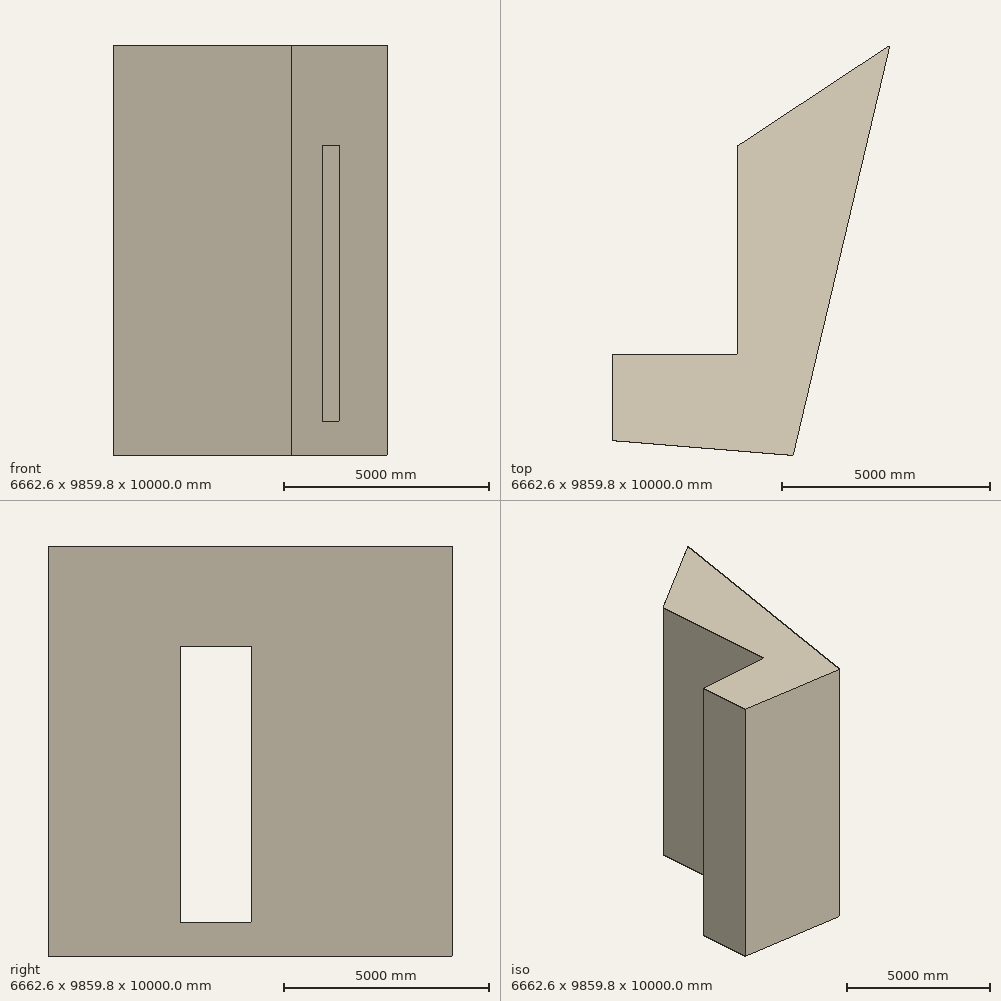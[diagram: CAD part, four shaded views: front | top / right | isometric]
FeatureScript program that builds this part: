
annotation { "Feature Type Name" : "Feature", "Feature Type Description" : "" }
export const myFeature = defineFeature(function(context is Context, id is Id, definition is map)
    precondition{}
    {
        {
            var Q0;
            Q0=qCreatedBy(makeId("Top.planeOp"),FACE);
            var sketch = newSketch(context, id + "F0", { "sketchPlane" : qUnion([Q0])});
            skLineSegment(sketch, "E0.bottom", {"start": v(-10975.18, 7041.84) * mm, "end": v(13954.74, 7041.84) * mm});
            skLineSegment(sketch, "E0.top", {"start": v(-13975.18, -7051.86) * mm, "end": v(13954.74, -7051.86) * mm});
            skLineSegment(sketch, "E0.left", {"start": v(-13975.18, 2041.84) * mm, "end": v(-13975.18, -7051.86) * mm});
            skLineSegment(sketch, "E0.right", {"start": v(13954.74, 7041.84) * mm, "end": v(13954.74, -7051.86) * mm});
            skLineSegment(sketch, "E1", {"start": v(-10975.18, 7041.84) * mm, "end": v(-10975.18, 2041.84) * mm});
            skLineSegment(sketch, "E2", {"start": v(-10975.18, 2041.84) * mm, "end": v(-13975.18, 2041.84) * mm});
            skLineSegment(sketch, "E3.bottom", {"start": v(-12681.6, 1707.23) * mm, "end": v(-3728.69, 1707.23) * mm});
            skLineSegment(sketch, "E3.top", {"start": v(-13445.3, -6384.52) * mm, "end": v(-3728.69, -6384.52) * mm});
            skLineSegment(sketch, "E3.left", {"start": v(-13445.3, 1037.52) * mm, "end": v(-13445.3, -6384.52) * mm});
            skLineSegment(sketch, "E3.right", {"start": v(-3728.69, 1707.23) * mm, "end": v(-3728.69, -6384.52) * mm});
            skLineSegment(sketch, "E4.top", {"start": v(-13445.3, 1037.52) * mm, "end": v(-12681.6, 1037.52) * mm});
            skLineSegment(sketch, "E4.right", {"start": v(-12681.6, 1707.23) * mm, "end": v(-12681.6, 1037.52) * mm});
            skLineSegment(sketch, "E5.bottom", {"start": v(-10479.56, 6707.58) * mm, "end": v(-6087.2, 6707.58) * mm});
            skLineSegment(sketch, "E5.top", {"start": v(-10479.56, 3636.61) * mm, "end": v(-6087.2, 3636.61) * mm});
            skLineSegment(sketch, "E5.left", {"start": v(-10479.56, 6707.58) * mm, "end": v(-10479.56, 3636.61) * mm});
            skLineSegment(sketch, "E5.right", {"start": v(-6087.2, 6707.58) * mm, "end": v(-6087.2, 3636.61) * mm});
            skLineSegment(sketch, "E6", {"start": v(-10479.56, 5878.9) * mm, "end": v(-6087.2, 5878.9) * mm, "construction": true});
            skLineSegment(sketch, "E7.bottom", {"start": v(-10479.56, 3050.1) * mm, "end": v(8796.89, 3050.1) * mm});
            skLineSegment(sketch, "E7.top", {"start": v(-10479.56, 2175.66) * mm, "end": v(8796.89, 2175.66) * mm});
            skLineSegment(sketch, "E7.left", {"start": v(-10479.56, 3050.1) * mm, "end": v(-10479.56, 2175.66) * mm});
            skLineSegment(sketch, "E7.right", {"start": v(8796.89, 3050.1) * mm, "end": v(8796.89, 2175.66) * mm});
            skSolve(sketch);
        }
        {
            var Q0;
            Q0=qCreatedBy(makeId("Top.planeOp"),FACE);
            var sketch = newSketch(context, id + "F1", { "sketchPlane" : qUnion([Q0])});
            skLineSegment(sketch, "E8.bottom", {"start": v(-13975.18, 2041.84) * mm, "end": v(-10975.18, 2041.84) * mm});
            skLineSegment(sketch, "E8.left", {"start": v(-13975.18, -39.92) * mm, "end": v(-13975.18, 2041.84) * mm});
            skLineSegment(sketch, "E8.right", {"start": v(-10975.18, 2041.84) * mm, "end": v(-10975.18, 7041.84) * mm});
            skLineSegment(sketch, "E9", {"start": v(-13975.18, -39.92) * mm, "end": v(-9640.02, -396.7) * mm});
            skLineSegment(sketch, "E10", {"start": v(-9640.02, -396.7) * mm, "end": v(-7312.54, 9463.06) * mm});
            skLineSegment(sketch, "E11", {"start": v(-7312.54, 9463.06) * mm, "end": v(-10975.18, 7041.84) * mm});
            skSolve(sketch);
        }
        {
            var Q0;
            Q0 = qSketchRegion(id + "F1", true);
            extrude(context, id + "F2", {"entities" : qUnion([Q0]), "depth" : 10000 * mm, "offsetDistance" : 25 * mm});
        }
        {
            var Q0;
            Q0=makeQuery(id+"F2.opExtrude","SWEPT_FACE",FACE,{"disambiguationData":[OSD([sQuery(id+"F1.wireOp",EDGE,"E8.right")])]});
            var sketch = newSketch(context, id + "F3", { "sketchPlane" : qUnion([Q0])});
            skLineSegment(sketch, "E12.bottom", {"start": v(-4550.06, 823.3) * mm, "end": v(-2822.45, 823.3) * mm});
            skLineSegment(sketch, "E12.top", {"start": v(-4550.06, 7552.55) * mm, "end": v(-2822.45, 7552.55) * mm});
            skLineSegment(sketch, "E12.left", {"start": v(-4550.06, 823.3) * mm, "end": v(-4550.06, 7552.55) * mm});
            skLineSegment(sketch, "E12.right", {"start": v(-2822.45, 823.3) * mm, "end": v(-2822.45, 7552.55) * mm});
            skSolve(sketch);
        }
        {
            var Q0;
            Q0 = qSketchRegion(id + "F3", true);
            extrude(context, id + "F4", {"entities" : qUnion([Q0]), "operationType" : NewBodyOperationType.REMOVE, "oppositeDirection" : true, "depth" : 14510 * mm, "offsetDistance" : 25 * mm});
        }
    });
